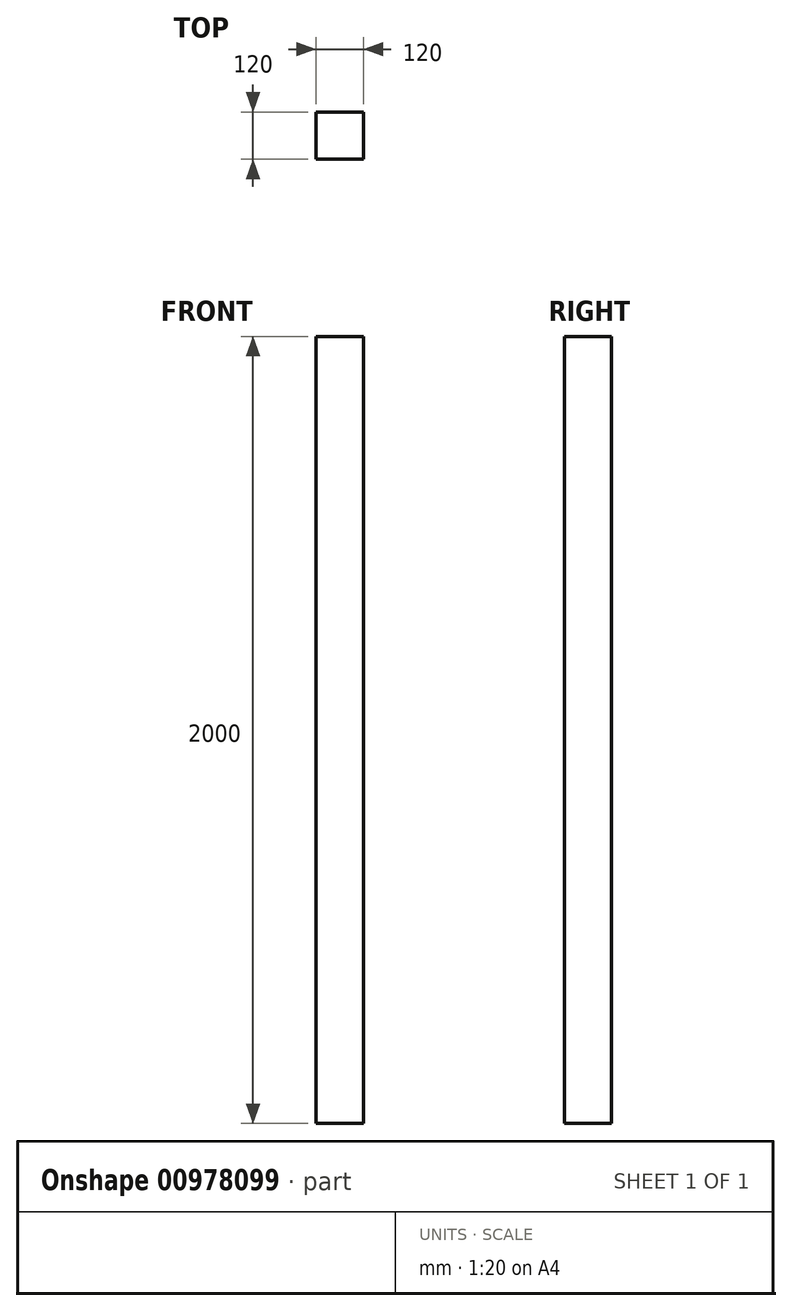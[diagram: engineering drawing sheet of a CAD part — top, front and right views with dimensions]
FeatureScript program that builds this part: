
annotation { "Feature Type Name" : "Feature", "Feature Type Description" : "" }
export const myFeature = defineFeature(function(context is Context, id is Id, definition is map)
    precondition{}
    {
        {
            var Q0;
            Q0=qCreatedBy(makeId("Top.planeOp"),FACE);
            var sketch = newSketch(context, id + "F0", { "sketchPlane" : qUnion([Q0])});
            skLineSegment(sketch, "E0.bottom", {"start": v(-60, 60) * mm, "end": v(60, 60) * mm});
            skLineSegment(sketch, "E0.top", {"start": v(-60, -60) * mm, "end": v(60, -60) * mm});
            skLineSegment(sketch, "E0.left", {"start": v(-60, 60) * mm, "end": v(-60, -60) * mm});
            skLineSegment(sketch, "E0.right", {"start": v(60, 60) * mm, "end": v(60, -60) * mm});
            skPoint(sketch, "E0.middle", {"position": v(0, 0) * mm});
            skSolve(sketch);
        }
        {
            var Q0;
            Q0 = qSketchRegion(id + "F0", true);
            extrude(context, id + "F1", {"entities" : qUnion([Q0]), "depth" : 2000 * mm, "offsetDistance" : 25 * mm});
        }
    });
